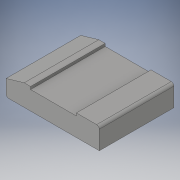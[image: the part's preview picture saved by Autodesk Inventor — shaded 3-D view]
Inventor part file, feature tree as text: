
AUTODESK INVENTOR PART (.ipt)
format: ipt  version: 2019 (Build 230136000, 136)  size: 129,536 bytes
history: native  units: in
note: dims shown in document units (in); Inventor stores cm internally (conversion verified against a paired STEP export)
features: extrude x3, sketch x3, fillet x1
ambient origin geometry x8: Origin, YZ Plane, XZ Plane, XY Plane, X Axis, Y Axis, Z Axis, Center Point
bodies: Solid1 (feature_tree)
feature tree (7):
  extrude  "Extrusion1"  Depth=3.5in
  extrude  "Extrusion2"  Depth=4.375in
  extrude  "Extrusion4"  Depth=1.075in
  fillet  "Fillet2"  Radius=0.125in
  sketch  "Sketch1"  dims[d0=4.375in d1=3.5in]
  sketch  "Sketch2"  dims[d2=1.0in d3=0.0in d4=4.375in]
  sketch  "Sketch4"  dims[d5=2.15in d6=1.075in d7=0.125in d8=0.0in d17=0.25in d18=0.3in d19=1.0in d20=0.0in d21=0.125in]
